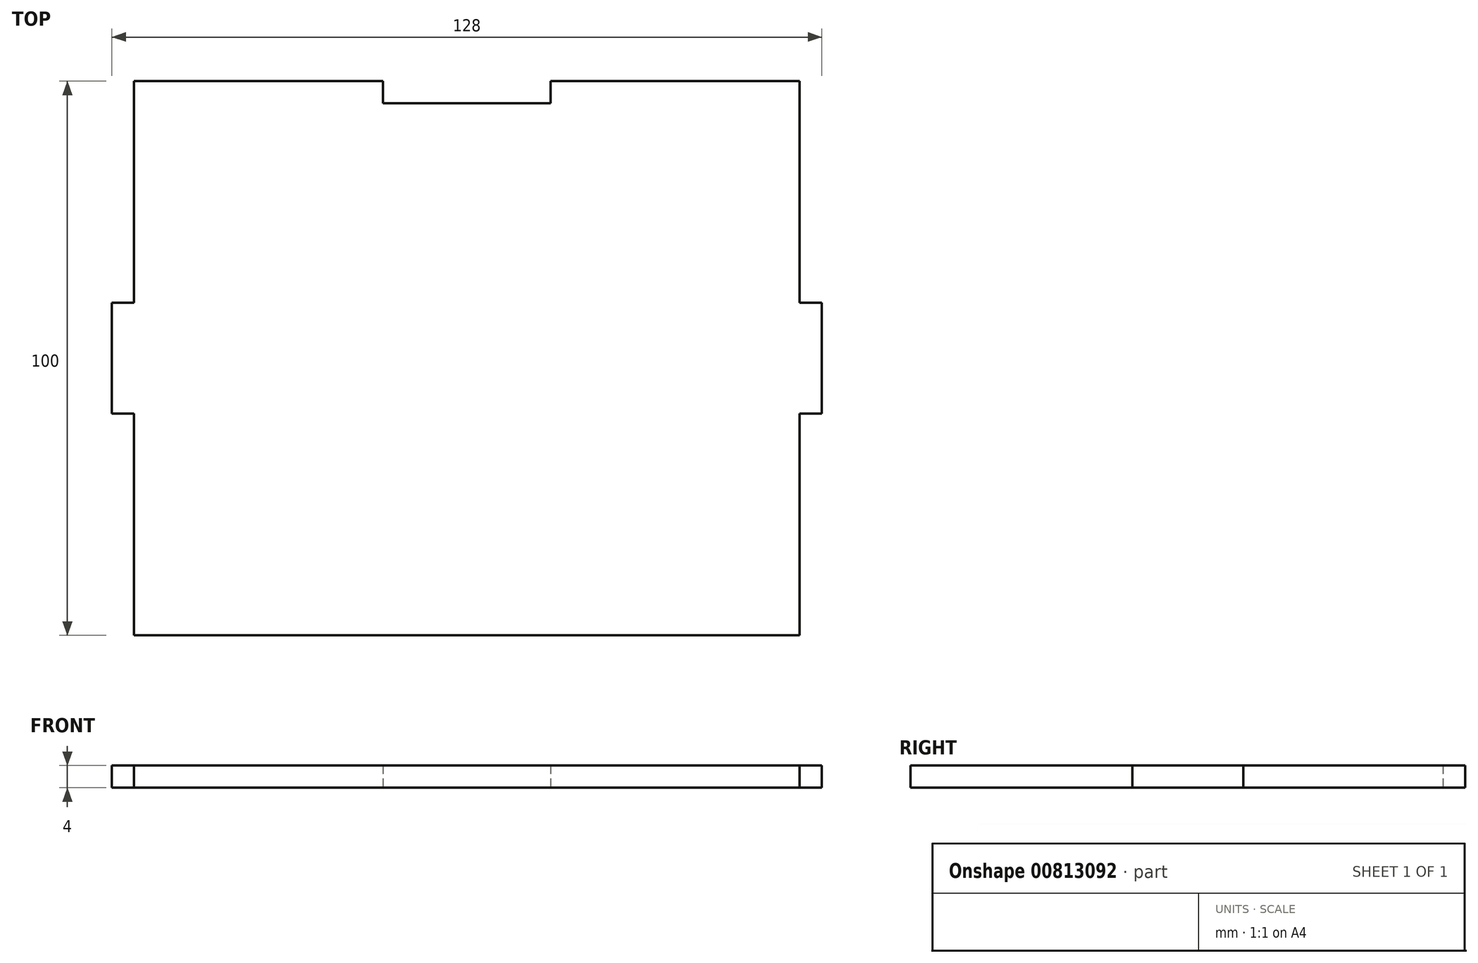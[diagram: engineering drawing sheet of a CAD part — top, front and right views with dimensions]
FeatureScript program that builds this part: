
annotation { "Feature Type Name" : "Feature", "Feature Type Description" : "" }
export const myFeature = defineFeature(function(context is Context, id is Id, definition is map)
    precondition{}
    {
        {
            var Q0;
            Q0=qCreatedBy(makeId("Top.planeOp"),FACE);
            var sketch = newSketch(context, id + "F0", { "sketchPlane" : qUnion([Q0])});
            skLineSegment(sketch, "E0.bottom", {"start": v(-60, 50) * mm, "end": v(-15.1, 50) * mm});
            skLineSegment(sketch, "E0.top", {"start": v(-60, -50) * mm, "end": v(60, -50) * mm});
            skLineSegment(sketch, "E0.left", {"start": v(-60, 50) * mm, "end": v(-60, 10) * mm});
            skLineSegment(sketch, "E0.right", {"start": v(60, 50) * mm, "end": v(60, 10) * mm});
            skPoint(sketch, "E0.middle", {"position": v(0, 0) * mm});
            skLineSegment(sketch, "E1.top", {"start": v(-15.1, 46) * mm, "end": v(15.1, 46) * mm});
            skLineSegment(sketch, "E1.left", {"start": v(-15.1, 50) * mm, "end": v(-15.1, 46) * mm});
            skLineSegment(sketch, "E1.right", {"start": v(15.1, 50) * mm, "end": v(15.1, 46) * mm});
            skPoint(sketch, "E1.middle", {"position": v(0, 48) * mm});
            skLineSegment(sketch, "E2.bottom", {"start": v(-64, 10) * mm, "end": v(-60, 10) * mm});
            skLineSegment(sketch, "E2.top", {"start": v(-64, -10) * mm, "end": v(-60, -10) * mm});
            skLineSegment(sketch, "E2.right", {"start": v(-64, 10) * mm, "end": v(-64, -10) * mm});
            skPoint(sketch, "E2.middle", {"position": v(-62, 0) * mm});
            skPoint(sketch, "E2.middle.positionSnap0", {"position": v(-60, 0) * mm});
            skPoint(sketch, "E2.centerSnap0", {"position": v(-60, 0) * mm});
            skPoint(sketch, "E3.MirrorP", {"position": v(60, 0) * mm});
            skPoint(sketch, "E4.MirrorP", {"position": v(62, 0) * mm});
            skLineSegment(sketch, "E5.MirrorCS", {"start": v(64, 10) * mm, "end": v(64, -10) * mm});
            skLineSegment(sketch, "E6.MirrorCS", {"start": v(64, -10) * mm, "end": v(60, -10) * mm});
            skLineSegment(sketch, "E7.MirrorCS", {"start": v(64, 10) * mm, "end": v(60, 10) * mm});
            skLineSegment(sketch, "E8.trimOffspring", {"start": v(-60, -10) * mm, "end": v(-60, -50) * mm});
            skLineSegment(sketch, "E9.trimOffspring", {"start": v(15.1, 50) * mm, "end": v(60, 50) * mm});
            skLineSegment(sketch, "E10.trimOffspring", {"start": v(60, -10) * mm, "end": v(60, -50) * mm});
            skSolve(sketch);
        }
        {
            var Q0;
            Q0=makeQuery(id+"F0.imprint","IMPRINT",FACE,{"disambiguationData":[TD([[makeQuery(id+"F0.imprint","IMPRINT",EDGE,{"derivedFrom":sQuery(id+"F0.wireOp",EDGE,"E0.bottom")}),-1.0]])]});
            extrude(context, id + "F1", {"entities" : qUnion([Q0]), "depth" : 4 * mm, "offsetDistance" : 25 * mm});
        }
    });
